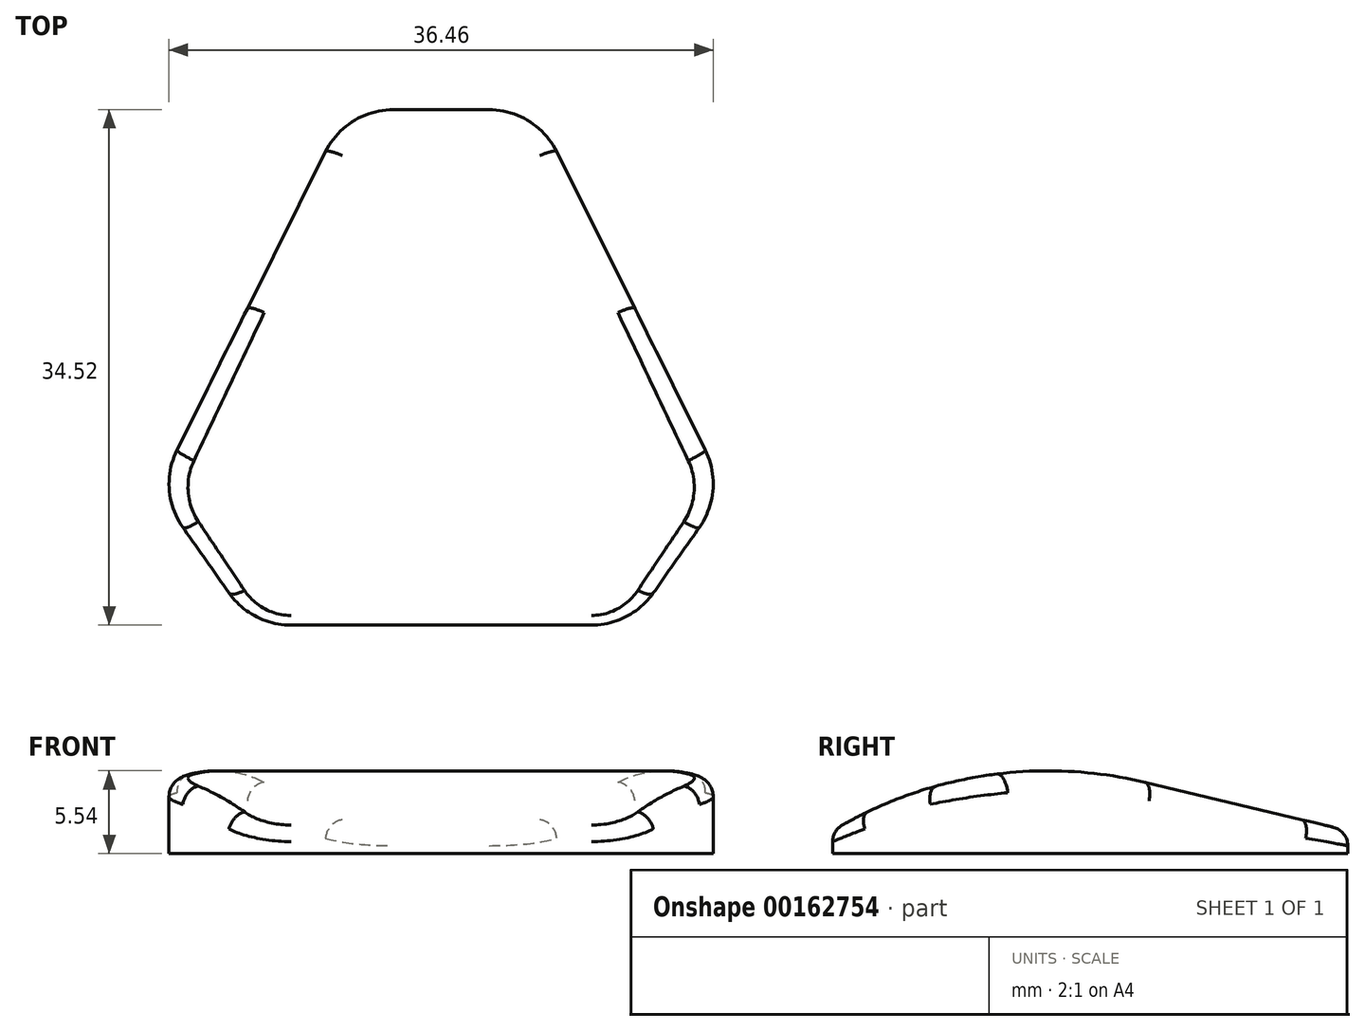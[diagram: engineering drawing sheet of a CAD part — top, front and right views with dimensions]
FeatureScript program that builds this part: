
annotation { "Feature Type Name" : "Feature", "Feature Type Description" : "" }
export const myFeature = defineFeature(function(context is Context, id is Id, definition is map)
    precondition{}
    {
        {
            var Q0;
            Q0=qCreatedBy(makeId("Top.planeOp"),FACE);
            var sketch = newSketch(context, id + "F0", { "sketchPlane" : qUnion([Q0])});
            skLineSegment(sketch, "E0", {"start": v(-12.7, -17.5) * mm, "end": v(12.7, -17.5) * mm});
            skLineSegment(sketch, "E1", {"start": v(12.7, -17.5) * mm, "end": v(19.05, -8.48) * mm});
            skLineSegment(sketch, "E2", {"start": v(19.05, -8.48) * mm, "end": v(6.35, 17.02) * mm});
            skLineSegment(sketch, "E3", {"start": v(6.35, 17.02) * mm, "end": v(-6.35, 17.02) * mm});
            skLineSegment(sketch, "E4", {"start": v(-6.35, 17.02) * mm, "end": v(-19.05, -8.48) * mm});
            skLineSegment(sketch, "E5", {"start": v(-19.05, -8.48) * mm, "end": v(-12.7, -17.5) * mm});
            skPoint(sketch, "E6", {"position": v(0, 17.02) * mm});
            skPoint(sketch, "E7", {"position": v(0, -17.5) * mm});
            skLineSegment(sketch, "E8", {"start": v(19.05, -8.48) * mm, "end": v(-19.05, -8.48) * mm, "construction": true});
            skSolve(sketch);
        }
        {
            var Q0;
            Q0=qSketchRegion(id+"F0",true);
            extrude(context, id + "F1", {"entities" : qUnion([Q0]), "depth" : 7.62 * mm});
        }
        {
            var Q0;
            Q0=makeQuery(id+"F1.opExtrude","CAP_EDGE",EDGE,{"disambiguationData":[OSD([sQuery(id+"F0.wireOp",EDGE,"E0")])],"isStart":false});
            chamfer(context, id + "F2", {"entities" : qUnion([Q0]), "chamferType" : ChamferType.TWO_OFFSETS, "width1" : 9.02 * mm, "oppositeDirection" : false, "width2" : 6.1 * mm, "tangentPropagation" : true});
        }
        {
            var Q0;
            Q0=makeQuery(id+"F1.opExtrude","CAP_EDGE",EDGE,{"disambiguationData":[OSD([sQuery(id+"F0.wireOp",EDGE,"E3")])],"isStart":false});
            chamfer(context, id + "F3", {"entities" : qUnion([Q0]), "chamferType" : ChamferType.TWO_OFFSETS, "width1" : 25.5 * mm, "oppositeDirection" : false, "width2" : 6.1 * mm, "tangentPropagation" : true});
        }
        {
            var Q0;
            Q0=makeQuery(id+"F1.opExtrude","SWEPT_EDGE",EDGE,{"disambiguationData":[OSD([sQuery(id+"F0.wireOp",EDGE,"E1"),sQuery(id+"F0.wireOp",EDGE,"E2")])]});
            var Q1;
            Q1=makeQuery(id+"F1.opExtrude","SWEPT_EDGE",EDGE,{"disambiguationData":[OSD([sQuery(id+"F0.wireOp",EDGE,"E0"),sQuery(id+"F0.wireOp",EDGE,"E1")])]});
            var Q2;
            Q2=makeQuery(id+"F1.opExtrude","SWEPT_EDGE",EDGE,{"disambiguationData":[OSD([sQuery(id+"F0.wireOp",EDGE,"E0"),sQuery(id+"F0.wireOp",EDGE,"E5")])]});
            var Q3;
            Q3=makeQuery(id+"F1.opExtrude","SWEPT_EDGE",EDGE,{"disambiguationData":[OSD([sQuery(id+"F0.wireOp",EDGE,"E4"),sQuery(id+"F0.wireOp",EDGE,"E5")])]});
            var Q4;
            Q4=makeQuery(id+"F1.opExtrude","SWEPT_EDGE",EDGE,{"disambiguationData":[OSD([sQuery(id+"F0.wireOp",EDGE,"E2"),sQuery(id+"F0.wireOp",EDGE,"E3")])]});
            var Q5;
            Q5=makeQuery(id+"F1.opExtrude","SWEPT_EDGE",EDGE,{"disambiguationData":[OSD([sQuery(id+"F0.wireOp",EDGE,"E3"),sQuery(id+"F0.wireOp",EDGE,"E4")])]});
            fillet(context, id + "F4", {"entities" : qUnion([Q0, Q1, Q2, Q3, Q4, Q5]), "radius" : 5.08 * mm, "tangentPropagation" : true, "allowEdgeOverflow" : false});
        }
        {
            var Q0;
            Q0=makeQuery(id+"F3.opChamfer","BLEND_EDGE",EDGE,{"blendedFrom":[makeQuery(id+"F1.opExtrude","CAP_EDGE",EDGE,{"disambiguationData":[OSD([sQuery(id+"F0.wireOp",EDGE,"E3")])],"isStart":false}),makeQuery(id+"F2.opChamfer","BLEND_FACE",FACE,{"disambiguationData":[OSD([sQuery(id+"F0.wireOp",EDGE,"E0")])]})],"blendedInto":[makeQuery(id+"F2.opChamfer","BLEND_FACE",FACE,{"disambiguationData":[OSD([sQuery(id+"F0.wireOp",EDGE,"E0")])]})]});
            fillet(context, id + "F5", {"entities" : qUnion([Q0]), "radius" : 27.94 * mm, "tangentPropagation" : true, "allowEdgeOverflow" : false});
        }
        {
            var Q0;
            {var subQ0=sQuery(id+"F0.wireOp",EDGE,"E0");Q0=makeQuery(id+"F5.opFillet","BLEND_EDGE",EDGE,{"blendedFrom":[makeQuery(id+"F3.opChamfer","BLEND_EDGE",EDGE,{"blendedFrom":[makeQuery(id+"F1.opExtrude","CAP_EDGE",EDGE,{"disambiguationData":[OSD([sQuery(id+"F0.wireOp",EDGE,"E3")])],"isStart":false}),makeQuery(id+"F2.opChamfer","BLEND_FACE",FACE,{"disambiguationData":[OSD([subQ0])]})],"blendedInto":[makeQuery(id+"F2.opChamfer","BLEND_FACE",FACE,{"disambiguationData":[OSD([subQ0])]})]}),makeQuery(id+"F1.opExtrude","SWEPT_FACE",FACE,{"disambiguationData":[OSD([subQ0])]})],"blendedInto":[makeQuery(id+"F1.opExtrude","SWEPT_FACE",FACE,{"disambiguationData":[OSD([subQ0])]})]});}
            fillet(context, id + "F6", {"entities" : qUnion([Q0]), "radius" : 1.27 * mm, "tangentPropagation" : true, "allowEdgeOverflow" : false});
        }
    });
